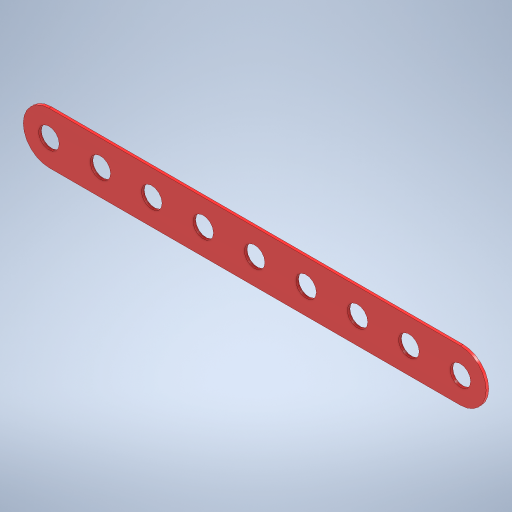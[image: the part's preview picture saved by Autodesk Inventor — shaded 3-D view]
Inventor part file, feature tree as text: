
AUTODESK INVENTOR PART (.ipt)
format: ipt  version: 2024 (Build 280153000, 153)  size: 257,536 bytes
history: native  units: mm
features: extrude x2, sketch x2, other x1, pattern_linear x1
ambient origin geometry x8: Origin, YZ Plane, XZ Plane, XY Plane, X Axis, Y Axis, Z Axis, Center Point
bodies: Body1 (feature_tree)
feature tree (6):
  other  "Těleso1"
  extrude  "Vysunutí1"  Depth=45.0mm
  extrude  "Vysunutí2"  Depth=5.0mm
  pattern_linear  "Obdélníkové pole1"  Spacing1=0.5mm  [1 undecoded]
  sketch  "Náčrt1"
  sketch  "Náčrt2"
note: 1 required parameter value undecoded (feature->parameter linkage not recoverable at this tier; creation-order binding heuristic only, values carry confidence <= 0.55)
